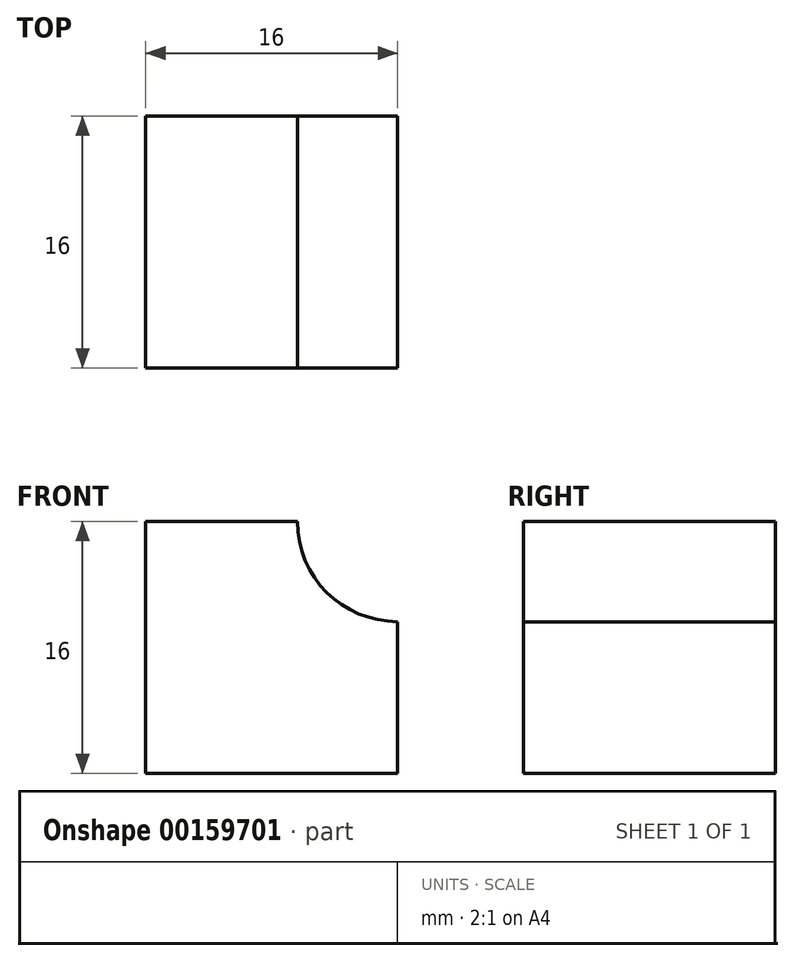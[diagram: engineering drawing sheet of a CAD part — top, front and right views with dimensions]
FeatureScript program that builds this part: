
annotation { "Feature Type Name" : "Feature", "Feature Type Description" : "" }
export const myFeature = defineFeature(function(context is Context, id is Id, definition is map)
    precondition{}
    {
        {
            var Q0;
            Q0=qCreatedBy(makeId("Front.planeOp"),FACE);
            var sketch = newSketch(context, id + "F0", { "sketchPlane" : qUnion([Q0])});
            skLineSegment(sketch, "E0.bottom", {"start": v(1.64, 8) * mm, "end": v(-8, 8) * mm});
            skLineSegment(sketch, "E0.top", {"start": v(8, -8) * mm, "end": v(-8, -8) * mm});
            skLineSegment(sketch, "E0.left", {"start": v(8, 1.64) * mm, "end": v(8, -8) * mm});
            skLineSegment(sketch, "E0.right", {"start": v(-8, 8) * mm, "end": v(-8, -8) * mm});
            skPoint(sketch, "E0.middle", {"position": v(0, 0) * mm});
            skArc(sketch, "E1", {"start": v(1.64, 8) * mm, "mid": v(3.5, 3.5) * mm, "end": v(8, 1.64) * mm});
            skSolve(sketch);
        }
        {
            var Q0;
            Q0 = qSketchRegion(id + "F0", true);
            extrude(context, id + "F1", {"entities" : qUnion([Q0]), "depth" : 16 * mm});
        }
    });
